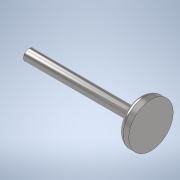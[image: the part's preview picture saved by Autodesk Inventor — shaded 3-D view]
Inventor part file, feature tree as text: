
AUTODESK INVENTOR PART (.ipt)
format: ipt  version: 2022 (Build 260153000, 153)  size: 127,488 bytes
history: native  units: in
note: dims shown in document units (in); Inventor stores cm internally (conversion verified against a paired STEP export)
features: extrude x2, fillet x2, sketch x2
ambient origin geometry x8: Origin, YZ Plane, XZ Plane, XY Plane, X Axis, Y Axis, Z Axis, Center Point
bodies: Solid1 (feature_tree)
feature tree (6):
  extrude  "Extrusion1"  Depth=7.874in TaperAngle=0.0deg
  extrude  "Extrusion2"  Depth=0.7874in TaperAngle=0.0deg
  fillet  "Fillet1"  Radius=0.3937in
  fillet  "Fillet2"  Radius=0.3937in
  sketch  "Sketch1"  dims[d0=0.7874in d1=7.874in d2=0.0in]
  sketch  "Sketch2"  dims[d3=3.1496in d4=0.7874in d5=0.0in d6=0.3937in d7=0.3937in]
